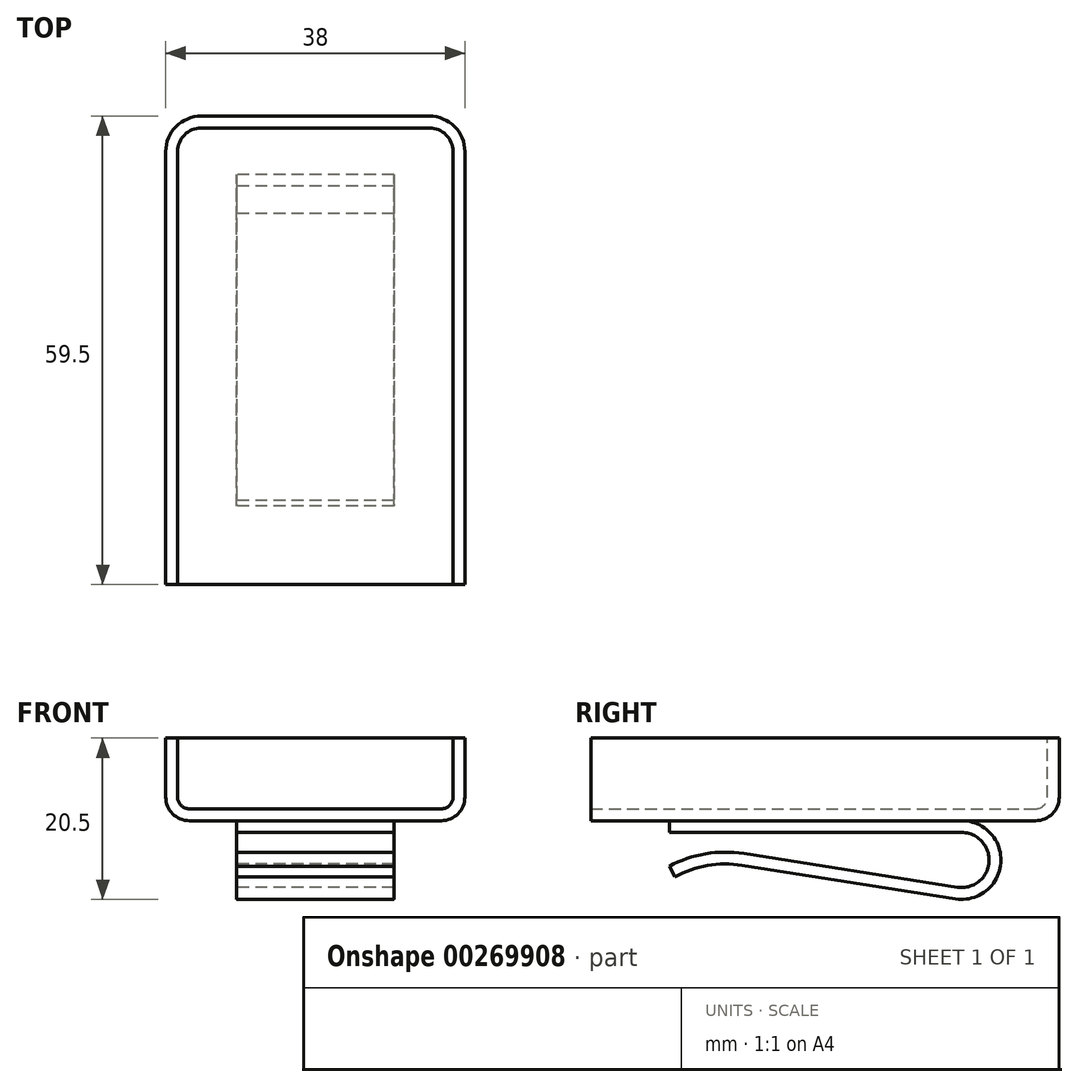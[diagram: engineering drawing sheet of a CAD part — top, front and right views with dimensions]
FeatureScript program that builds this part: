
annotation { "Feature Type Name" : "Feature", "Feature Type Description" : "" }
export const myFeature = defineFeature(function(context is Context, id is Id, definition is map)
    precondition{}
    {
        {
            var Q0;
            Q0=qCreatedBy(makeId("Top.planeOp"),FACE);
            var sketch = newSketch(context, id + "F0", { "sketchPlane" : qUnion([Q0])});
            skLineSegment(sketch, "E0.top", {"start": v(-19, 0) * mm, "end": v(19, 0) * mm});
            skLineSegment(sketch, "E1.0", {"start": v(-19, 59.5) * mm, "end": v(-19, 0) * mm});
            skLineSegment(sketch, "E1.1", {"start": v(-19, 59.5) * mm, "end": v(19, 59.5) * mm});
            skLineSegment(sketch, "E1.2", {"start": v(19, 59.5) * mm, "end": v(19, 0) * mm});
            skSolve(sketch);
        }
        {
            var Q0;
            Q0 = qSketchRegion(id + "F0", true);
            extrude(context, id + "F1", {"entities" : qUnion([Q0]), "depth" : 10.5 * mm});
        }
        {
            var Q0;
            Q0=makeQuery(id+"F1.opExtrude","CAP_EDGE",EDGE,{"disambiguationData":[OSD([sQuery(id+"F0.wireOp",EDGE,"E1.2")])],"isStart":true});
            var Q1;
            Q1=makeQuery(id+"F1.opExtrude","CAP_EDGE",EDGE,{"disambiguationData":[OSD([sQuery(id+"F0.wireOp",EDGE,"E1.1")])],"isStart":true});
            var Q2;
            Q2=makeQuery(id+"F1.opExtrude","CAP_EDGE",EDGE,{"disambiguationData":[OSD([sQuery(id+"F0.wireOp",EDGE,"E1.0")])],"isStart":true});
            fillet(context, id + "F2", {"entities" : qUnion([Q0, Q1, Q2]), "radius" : 3 * mm, "tangentPropagation" : true, "allowEdgeOverflow" : false});
        }
        {
            var Q0;
            Q0=makeQuery(id+"F1.opExtrude","SWEPT_EDGE",EDGE,{"disambiguationData":[OSD([sQuery(id+"F0.wireOp",EDGE,"E1.1"),sQuery(id+"F0.wireOp",EDGE,"E1.2")])]});
            var Q1;
            Q1=makeQuery(id+"F1.opExtrude","SWEPT_EDGE",EDGE,{"disambiguationData":[OSD([sQuery(id+"F0.wireOp",EDGE,"E1.0"),sQuery(id+"F0.wireOp",EDGE,"E1.1")])]});
            fillet(context, id + "F3", {"entities" : qUnion([Q0, Q1]), "radius" : 4.5 * mm, "tangentPropagation" : true, "allowEdgeOverflow" : false});
        }
        {
            var Q0;
            Q0=makeQuery(id+"F1.opExtrude","SWEPT_FACE",FACE,{"disambiguationData":[OSD([sQuery(id+"F0.wireOp",EDGE,"E0.top")])]});
            var Q1;
            Q1=makeQuery(id+"F1.opExtrude","CAP_FACE",FACE,{"disambiguationData":[OSD([sQuery(id+"F0.wireOp",EDGE,"E0.top"),sQuery(id+"F0.wireOp",EDGE,"E1.0"),sQuery(id+"F0.wireOp",EDGE,"E1.1"),sQuery(id+"F0.wireOp",EDGE,"E1.2")])],"isStart":false});
            shell(context, id + "F4", {"entities" : qUnion([Q0, Q1]), "thickness" : 1.5 * mm});
        }
        {
            var Q0;
            Q0=qCreatedBy(makeId("Right.planeOp"),FACE);
            var sketch = newSketch(context, id + "F5", { "sketchPlane" : qUnion([Q0])});
            skLineSegment(sketch, "E2.0", {"start": v(55, 0) * mm, "end": v(0, 0) * mm, "construction": true});
            skArc(sketch, "E3", {"start": v(47.1, 0) * mm, "mid": v(52.08, -5.4) * mm, "end": v(46.32, -9.94) * mm});
            skLineSegment(sketch, "E4", {"start": v(46.32, -9.94) * mm, "end": v(19.2, -5.66) * mm});
            skArc(sketch, "E5", {"start": v(19.2, -5.66) * mm, "mid": v(14.82, -5.7) * mm, "end": v(10.69, -7.12) * mm});
            skArc(sketch, "E6.0", {"start": v(19.43, -4.18) * mm, "mid": v(14.57, -4.21) * mm, "end": v(9.98, -5.8) * mm});
            skLineSegment(sketch, "E6.1", {"start": v(46.55, -8.46) * mm, "end": v(19.43, -4.18) * mm});
            skArc(sketch, "E6.2", {"start": v(47.1, -1.5) * mm, "mid": v(50.58, -5.27) * mm, "end": v(46.55, -8.46) * mm});
            skLineSegment(sketch, "E7", {"start": v(47.1, -1.5) * mm, "end": v(9.98, -1.5) * mm});
            skLineSegment(sketch, "E8", {"start": v(9.98, -1.5) * mm, "end": v(9.98, 0) * mm});
            skLineSegment(sketch, "E9", {"start": v(9.98, 0) * mm, "end": v(47.1, 0) * mm});
            skLineSegment(sketch, "E10", {"start": v(9.98, -5.8) * mm, "end": v(10.69, -7.12) * mm});
            skSolve(sketch);
        }
        {
            var Q0;
            Q0 = qSketchRegion(id + "F5", true);
            extrude(context, id + "F6", {"entities" : qUnion([Q0]), "operationType" : NewBodyOperationType.ADD, "depth" : 20 * mm, "symmetric" : true});
        }
    });
